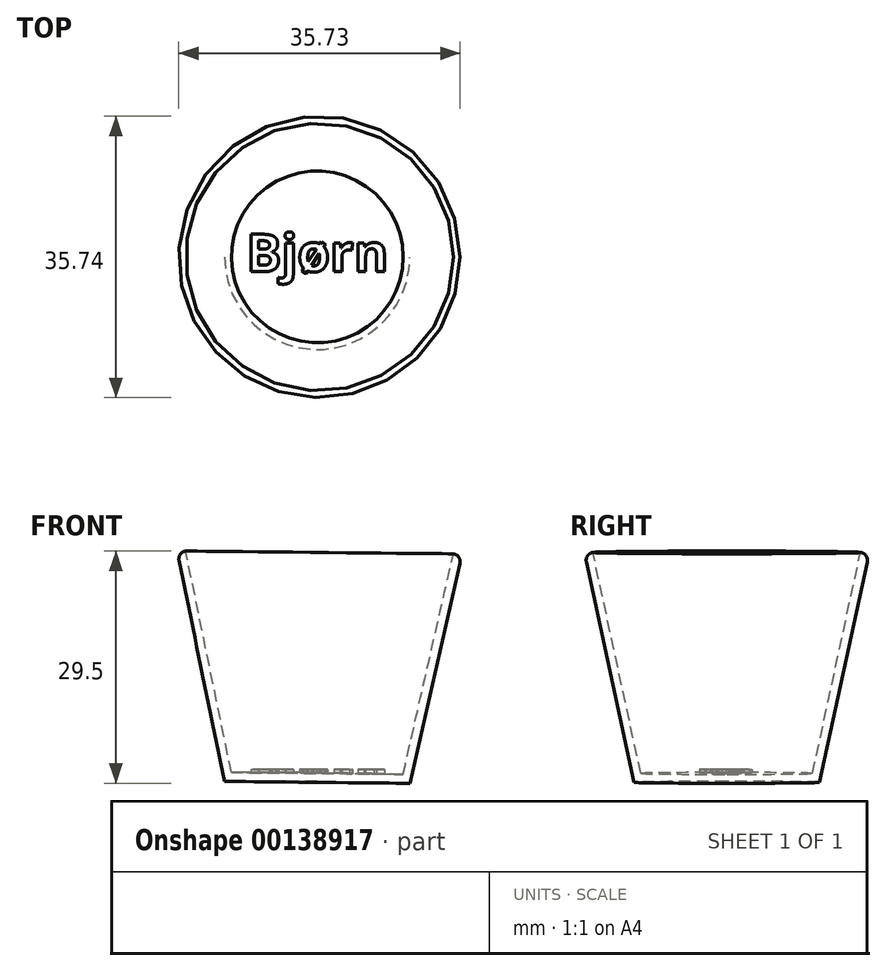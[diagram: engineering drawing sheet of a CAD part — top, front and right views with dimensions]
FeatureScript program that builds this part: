
annotation { "Feature Type Name" : "Feature", "Feature Type Description" : "" }
export const myFeature = defineFeature(function(context is Context, id is Id, definition is map)
    precondition{}
    {
        {
            var Q0;
            Q0=qCreatedBy(makeId("Front.planeOp"),FACE);
            var sketch = newSketch(context, id + "F0", { "sketchPlane" : qUnion([Q0])});
            skLineSegment(sketch, "E0", {"start": v(0, 0) * mm, "end": v(-11.78, 0) * mm});
            skLineSegment(sketch, "E1", {"start": v(-11.78, 0) * mm, "end": v(-17.82, 29.26) * mm});
            skLineSegment(sketch, "E2", {"start": v(-17.82, 29.26) * mm, "end": v(-16.7, 29.26) * mm});
            skLineSegment(sketch, "E3", {"start": v(-16.7, 29.26) * mm, "end": v(-10.9, 1.13) * mm});
            skLineSegment(sketch, "E4", {"start": v(-10.9, 1.13) * mm, "end": v(0, 1.13) * mm});
            skLineSegment(sketch, "E5", {"start": v(0, 1.13) * mm, "end": v(-0.01, -0.15) * mm});
            skSolve(sketch);
        }
        {
            var Q0;
            Q0 = qSketchRegion(id + "F0", true);
            var Q1;
            Q1=sQuery(id+"F0.wireOp",EDGE,"E5");
            revolve(context, id + "F1", {"entities" : qUnion([Q0]), "axis" : qUnion([Q1]), "revolveType" : RevolveType.FULL});
        }
        {
            var Q0;
            Q0=makeQuery(id+"F1.opRevolve","SWEPT_EDGE",EDGE,{"disambiguationData":[OSD([sQuery(id+"F0.wireOp",EDGE,"E1"),sQuery(id+"F0.wireOp",EDGE,"E2")])]});
            fillet(context, id + "F2", {"entities" : qUnion([Q0]), "radius" : 1 * mm, "tangentPropagation" : true, "allowEdgeOverflow" : false});
        }
        {
            var Q0;
            Q0=qCreatedBy(makeId("Top.planeOp"),FACE);
            var sketch = newSketch(context, id + "F3", { "sketchPlane" : qUnion([Q0])});
            skText(sketch, "E6", { "text": "Bjørn", "fontName": "OpenSans-Bold.ttf"});
            const initialGuessF3  = {"E6": [-0.00904, -0.00188, 1, 0, 0.0048]};
            skSetInitialGuess(sketch, initialGuessF3);
            skSolve(sketch);
        }
        {
            var Q0;
            Q0 = qSketchRegion(id + "F3", true);
            extrude(context, id + "F4", {"entities" : qUnion([Q0]), "operationType" : NewBodyOperationType.ADD, "depth" : 1.5 * mm});
        }
    });
